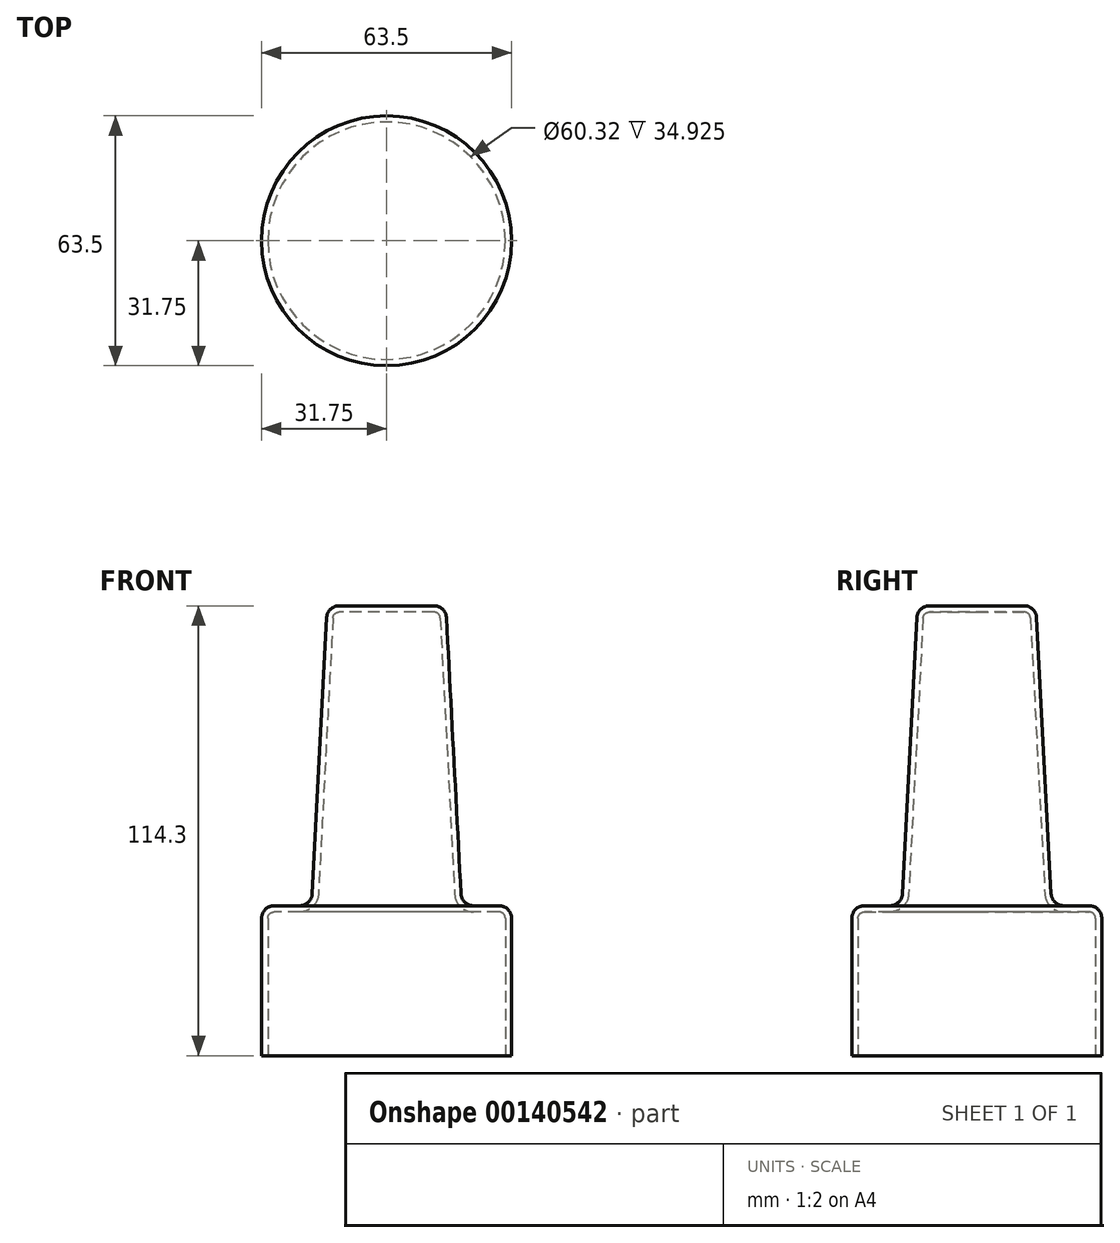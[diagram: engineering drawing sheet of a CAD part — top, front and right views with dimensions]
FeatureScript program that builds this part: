
annotation { "Feature Type Name" : "Feature", "Feature Type Description" : "" }
export const myFeature = defineFeature(function(context is Context, id is Id, definition is map)
    precondition{}
    {
        {
            var Q0;
            Q0=qCreatedBy(makeId("Top.planeOp"),FACE);
            var sketch = newSketch(context, id + "F3", { "sketchPlane" : qUnion([Q0])});
            skCircle(sketch, "E0", {"center": v(0, 0) * mm, "radius": 31.75 * mm});
            skSolve(sketch);
        }
        {
            var Q0;
            Q0=qSketchRegion(id+"F3",true);
            extrude(context, id + "F0", {"entities" : qUnion([Q0]), "depth" : 38.1 * mm});
        }
        {
            var Q0;
            Q0=makeQuery(id+"F0.opExtrude","CAP_FACE",FACE,{"disambiguationData":[OSD([sQuery(id+"F3.wireOp",EDGE,"E0")])],"isStart":false});
            var sketch = newSketch(context, id + "F1", { "sketchPlane" : qUnion([Q0])});
            skCircle(sketch, "E1", {"center": v(0, 0) * mm, "radius": 19.05 * mm});
            skSolve(sketch);
        }
        {
            var Q0;
            Q0=qSketchRegion(id+"F1",true);
            extrude(context, id + "F4", {"entities" : qUnion([Q0]), "operationType" : NewBodyOperationType.ADD, "depth" : 76.2 * mm, "hasDraft" : true, "draftAngle" : 3 * degree, "draftPullDirection" : true});
        }
        {
            var Q0;
            Q0=makeQuery(id+"F4.opExtrude","SWEPT_FACE",FACE,{"disambiguationData":[OSD([sQuery(id+"F1.wireOp",EDGE,"E1")])]});
            var Q1;
            Q1=makeQuery(id+"F0.opExtrude","CAP_EDGE",EDGE,{"disambiguationData":[OSD([sQuery(id+"F3.wireOp",EDGE,"E0")])],"isStart":false});
            fillet(context, id + "F2", {"entities" : qUnion([Q0, Q1]), "radius" : 3.17 * mm, "tangentPropagation" : true, "allowEdgeOverflow" : false});
        }
        {
            var Q0;
            Q0=makeQuery(id+"F0.opExtrude","CAP_FACE",FACE,{"disambiguationData":[OSD([sQuery(id+"F3.wireOp",EDGE,"E0")])],"isStart":true});
            shell(context, id + "F5", {"entities" : qUnion([Q0]), "thickness" : 1.59 * mm});
        }
    });
